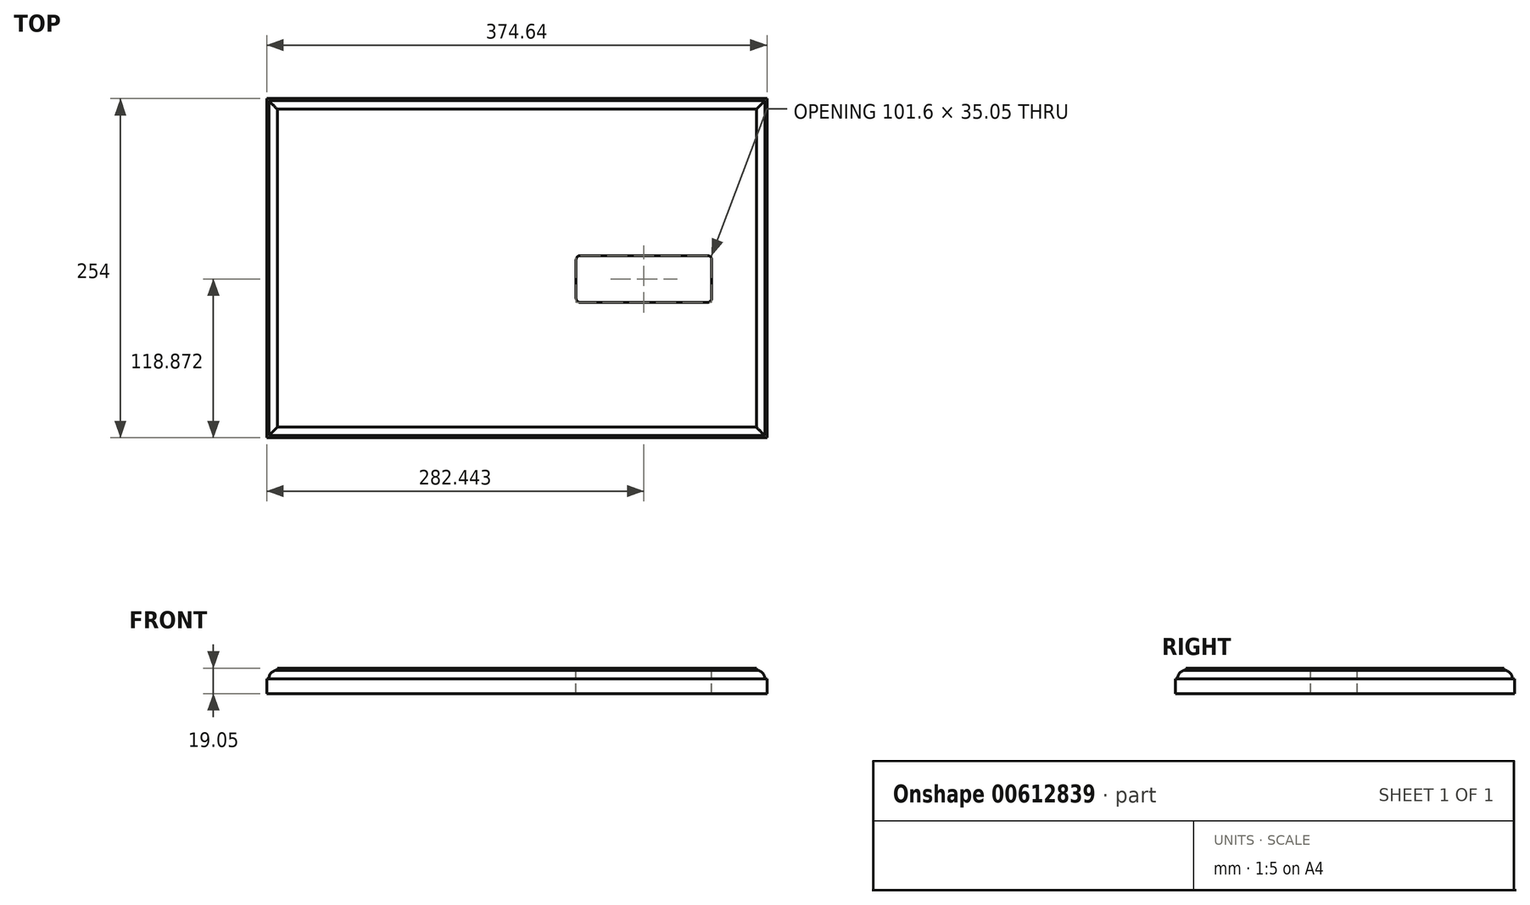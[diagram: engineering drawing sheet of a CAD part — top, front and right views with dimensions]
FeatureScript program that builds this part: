
annotation { "Feature Type Name" : "Feature", "Feature Type Description" : "" }
export const myFeature = defineFeature(function(context is Context, id is Id, definition is map)
    precondition{}
    {
        {
            var Q0;
            Q0=qCreatedBy(makeId("Top.planeOp"),FACE);
            var sketch = newSketch(context, id + "F0", { "sketchPlane" : qUnion([Q0])});
            skLineSegment(sketch, "E0.rect.bottom", {"start": v(187.33, -127) * mm, "end": v(-187.33, -127) * mm});
            skLineSegment(sketch, "E0.rect.top", {"start": v(187.33, 127) * mm, "end": v(-187.33, 127) * mm});
            skLineSegment(sketch, "E0.rect.left", {"start": v(187.33, -127) * mm, "end": v(187.33, 127) * mm});
            skLineSegment(sketch, "E0.rect.right", {"start": v(-187.33, -127) * mm, "end": v(-187.33, 127) * mm});
            skPoint(sketch, "E0.rect.middle", {"position": v(0, 0) * mm});
            skLineSegment(sketch, "E1.rect.bottom", {"start": v(142.75, 9.4) * mm, "end": v(47.5, 9.4) * mm});
            skLineSegment(sketch, "E1.rect.top", {"start": v(142.75, -25.65) * mm, "end": v(47.5, -25.65) * mm});
            skLineSegment(sketch, "E1.rect.left", {"start": v(145.92, 6.22) * mm, "end": v(145.92, -22.48) * mm});
            skLineSegment(sketch, "E1.rect.right", {"start": v(44.32, 6.22) * mm, "end": v(44.32, -22.48) * mm});
            skPoint(sketch, "E1.rect.middle", {"position": v(95.12, -8.13) * mm});
            skPoint(sketch, "E2.visualSharp", {"position": v(44.32, 9.4) * mm});
            skArc(sketch, "E2.filletArc", {"start": v(47.5, 9.4) * mm, "mid": v(45.25, 8.47) * mm, "end": v(44.32, 6.22) * mm});
            skPoint(sketch, "E3.visualSharp", {"position": v(145.92, 9.4) * mm});
            skArc(sketch, "E3.filletArc", {"start": v(145.92, 6.22) * mm, "mid": v(145, 8.47) * mm, "end": v(142.75, 9.4) * mm});
            skPoint(sketch, "E4.visualSharp", {"position": v(145.92, -25.65) * mm});
            skArc(sketch, "E4.filletArc", {"start": v(142.75, -25.65) * mm, "mid": v(145, -24.72) * mm, "end": v(145.92, -22.48) * mm});
            skPoint(sketch, "E5.visualSharp", {"position": v(44.32, -25.65) * mm});
            skArc(sketch, "E5.filletArc", {"start": v(44.32, -22.48) * mm, "mid": v(45.25, -24.72) * mm, "end": v(47.5, -25.65) * mm});
            skSolve(sketch);
        }
        {
            var Q0;
            Q0=qSketchRegion(id+"F0",true);
            extrude(context, id + "F1", {"entities" : qUnion([Q0]), "oppositeDirection" : true, "depth" : 19.05 * mm});
        }
        {
            var Q0;
            Q0=qCreatedBy(makeId("Front.planeOp"),FACE);
            var sketch = newSketch(context, id + "F2", { "sketchPlane" : qUnion([Q0])});
            skLineSegment(sketch, "E6", {"start": v(179.37, 0) * mm, "end": v(179.37, -1.6) * mm});
            skLineSegment(sketch, "E7", {"start": v(187.33, -7.95) * mm, "end": v(185.72, -7.95) * mm});
            skArc(sketch, "E8", {"start": v(185.72, -7.95) * mm, "mid": v(183.86, -3.46) * mm, "end": v(179.37, -1.6) * mm});
            skLineSegment(sketch, "E9", {"start": v(179.37, 0) * mm, "end": v(187.33, 0) * mm});
            skLineSegment(sketch, "E10", {"start": v(187.33, 0) * mm, "end": v(187.33, -7.95) * mm});
            skLineSegment(sketch, "E11.MirrorCS", {"start": v(-179.37, 0) * mm, "end": v(-179.37, -1.6) * mm});
            skLineSegment(sketch, "E12.MirrorCS", {"start": v(-187.33, -7.95) * mm, "end": v(-185.72, -7.95) * mm});
            skArc(sketch, "E13.MirrorCS", {"start": v(-185.72, -7.95) * mm, "mid": v(-183.86, -3.46) * mm, "end": v(-179.37, -1.6) * mm});
            skLineSegment(sketch, "E14.MirrorCS", {"start": v(-179.37, 0) * mm, "end": v(-187.33, 0) * mm});
            skLineSegment(sketch, "E15.MirrorCS", {"start": v(-187.33, 0) * mm, "end": v(-187.33, -7.95) * mm});
            skSolve(sketch);
        }
        {
            var Q0;
            Q0=qSketchRegion(id+"F2",true);
            extrude(context, id + "F3", {"entities" : qUnion([Q0]), "operationType" : NewBodyOperationType.REMOVE, "oppositeDirection" : true, "depth" : 304.8 * mm, "symmetric" : true});
        }
        {
            var Q0;
            Q0=qCreatedBy(makeId("Right.planeOp"),FACE);
            var sketch = newSketch(context, id + "F4", { "sketchPlane" : qUnion([Q0])});
            skLineSegment(sketch, "E16", {"start": v(119.05, 0) * mm, "end": v(119.05, -1.6) * mm});
            skLineSegment(sketch, "E17", {"start": v(127, -7.95) * mm, "end": v(125.4, -7.95) * mm});
            skArc(sketch, "E18", {"start": v(125.4, -7.95) * mm, "mid": v(123.54, -3.46) * mm, "end": v(119.05, -1.6) * mm});
            skLineSegment(sketch, "E19", {"start": v(119.05, 0) * mm, "end": v(127, 0) * mm});
            skLineSegment(sketch, "E20", {"start": v(127, 0) * mm, "end": v(127, -7.95) * mm});
            skLineSegment(sketch, "E21.MirrorCS", {"start": v(-119.05, 0) * mm, "end": v(-119.05, -1.6) * mm});
            skArc(sketch, "E22.MirrorCS", {"start": v(-125.4, -7.95) * mm, "mid": v(-123.54, -3.46) * mm, "end": v(-119.05, -1.6) * mm});
            skLineSegment(sketch, "E23.MirrorCS", {"start": v(-127, -7.95) * mm, "end": v(-125.4, -7.95) * mm});
            skLineSegment(sketch, "E24.MirrorCS", {"start": v(-119.05, 0) * mm, "end": v(-127, 0) * mm});
            skLineSegment(sketch, "E25.MirrorCS", {"start": v(-127, 0) * mm, "end": v(-127, -7.95) * mm});
            skSolve(sketch);
        }
        {
            var Q0;
            Q0=qSketchRegion(id+"F4",true);
            extrude(context, id + "F5", {"entities" : qUnion([Q0]), "operationType" : NewBodyOperationType.REMOVE, "oppositeDirection" : true, "depth" : 406.4 * mm, "symmetric" : true});
        }
    });
